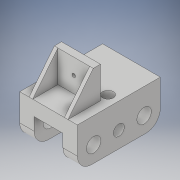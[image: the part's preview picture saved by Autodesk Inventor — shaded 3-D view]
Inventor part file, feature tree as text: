
AUTODESK INVENTOR PART (.ipt)
format: ipt  version: 2019 (Build 230136000, 136)  size: 217,600 bytes
history: native  units: mm
features: sketch x7, extrude x6, hole x3, fillet x1
ambient origin geometry x8: Origin, YZ Plane, XZ Plane, XY Plane, X Axis, Y Axis, Z Axis, Center Point
bodies: Solid1 (feature_tree)
feature tree (17):
  extrude  "Extrusion1"  Depth=80.0mm
  extrude  "Extrusion11"  Depth=20.0mm
  sketch  "Sketch13"  dims[d57=115.0mm d58=37.5mm d59=0.0mm]
  hole  "Hole2"  [1 undecoded]
  hole  "Hole3"  [1 undecoded]
  hole  "Hole6"  [1 undecoded]
  fillet  "Fillet19"  Radius=10.0mm
  extrude  "Extrusion15"  Depth=44.0mm TaperAngle=0.0deg
  extrude  "Extrusion16"  Depth=10.0mm TaperAngle=0.0deg
  extrude  "Extrusion18"  Depth=5.0mm
  extrude  "Extrusion19"  Depth=35.0mm
  sketch  "Sketch1"  dims[d0=115.0mm d1=80.0mm]
  sketch  "Sketch12"  dims[d2=20.0mm d3=0.0mm d56=20.0mm]
  sketch  "Sketch19"  dims[d63=20.0mm d64=6.0mm d65=4.0mm d66=2.0mm d67=90.0deg d68=8.0mm d69=20.594885mm]
  sketch  "Sketch20"  dims[d70=15.0mm d71=6.0mm d72=4.0mm d73=2.0mm d74=90.0deg d75=8.0mm d76=20.594885mm d111=25.0mm]
  sketch  "Sketch24"  dims[d112=25.0mm]
  sketch  "Sketch25"  dims[d113=15.0mm d114=6.0mm d115=4.0mm d116=2.0mm d117=90.0deg d118=15.0mm d119=0.0mm d120=20.0mm d122=10.0mm d123=44.0mm d124=0.0mm d126=50.0mm d127=0.0mm d128=5.0mm d129=35.0mm d130=35.0mm d131=15.0mm d132=22.0mm d136=40.0mm d138=360.0deg d151=45.0mm d152=54.0mm d155=5.0mm d156=5.0mm d157=44.0mm d158=0.0mm d159=100.0mm d160=0.0mm d161=10.0mm d12=1.0mm d13=1.0mm d14=1.0mm d15=0.15mm d16=0.25mm d17=0.375mm d18=14.3117mm d19=0.75mm d20=20.594885mm d21=0.0625mm d22=0.75mm d23=0.375mm]
note: 3 required parameter values undecoded (feature->parameter linkage not recoverable at this tier; creation-order binding heuristic only, values carry confidence <= 0.55)
